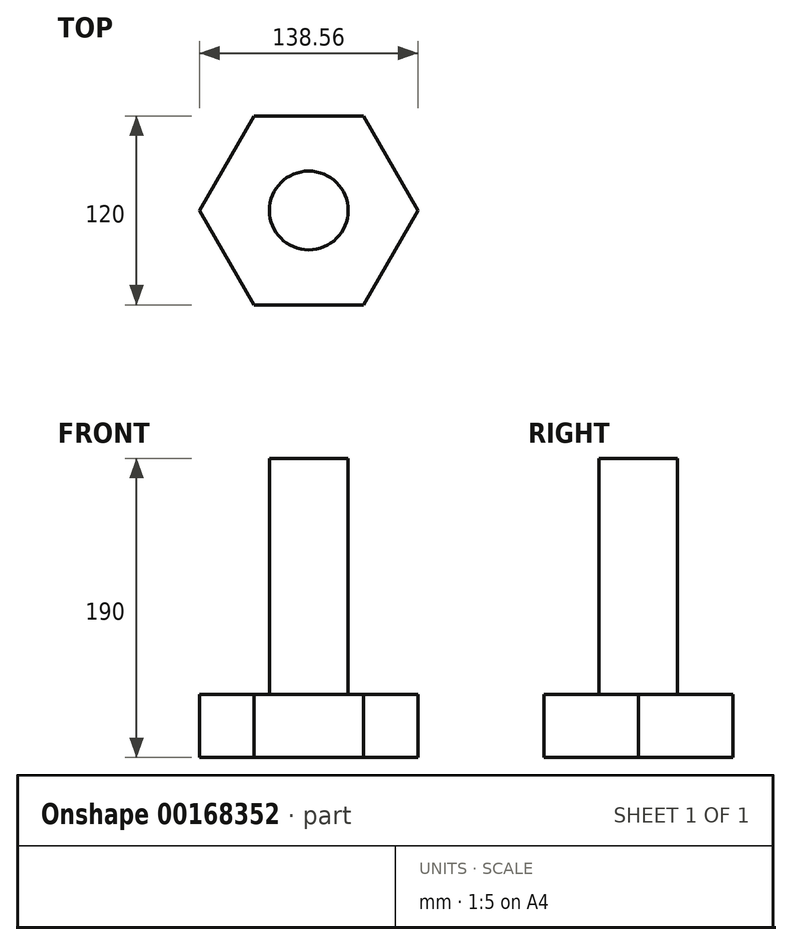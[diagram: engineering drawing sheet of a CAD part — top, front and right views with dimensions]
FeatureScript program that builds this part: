
annotation { "Feature Type Name" : "Feature", "Feature Type Description" : "" }
export const myFeature = defineFeature(function(context is Context, id is Id, definition is map)
    precondition{}
    {
        {
            var Q0;
            Q0=qCreatedBy(makeId("Top.planeOp"),FACE);
            var sketch = newSketch(context, id + "F0", { "sketchPlane" : qUnion([Q0])});
            skCircle(sketch, "E0.cCircle", {"center": v(0, 0) * mm, "radius": 60 * mm, "construction": true});
            skLineSegment(sketch, "E0.0", {"start": v(-34.64, 60) * mm, "end": v(34.64, 60) * mm});
            skLineSegment(sketch, "E0.1", {"start": v(34.64, 60) * mm, "end": v(69.28, 0) * mm});
            skLineSegment(sketch, "E0.2", {"start": v(69.28, 0) * mm, "end": v(34.64, -60) * mm});
            skLineSegment(sketch, "E0.3", {"start": v(34.64, -60) * mm, "end": v(-34.64, -60) * mm});
            skLineSegment(sketch, "E0.4", {"start": v(-34.64, -60) * mm, "end": v(-69.28, 0) * mm});
            skLineSegment(sketch, "E0.5", {"start": v(-69.28, 0) * mm, "end": v(-34.64, 60) * mm});
            skPoint(sketch, "E0.0.midPoint", {"position": v(0, 60) * mm});
            skSolve(sketch);
        }
        {
            var Q0;
            Q0=qSketchRegion(id+"F0",true);
            extrude(context, id + "F1", {"entities" : qUnion([Q0]), "depth" : 40 * mm});
        }
        {
            var Q0;
            Q0=makeQuery(id+"F1.opExtrude","CAP_FACE",FACE,{"disambiguationData":[OSD([sQuery(id+"F0.wireOp",EDGE,"E0.0"),sQuery(id+"F0.wireOp",EDGE,"E0.1"),sQuery(id+"F0.wireOp",EDGE,"E0.2"),sQuery(id+"F0.wireOp",EDGE,"E0.3"),sQuery(id+"F0.wireOp",EDGE,"E0.4"),sQuery(id+"F0.wireOp",EDGE,"E0.5")])],"isStart":false});
            var sketch = newSketch(context, id + "F2", { "sketchPlane" : qUnion([Q0])});
            skCircle(sketch, "E1", {"center": v(0, 0) * mm, "radius": 25 * mm});
            skSolve(sketch);
        }
        {
            var Q0;
            Q0=makeQuery(id+"F2.imprint","IMPRINT",FACE,{"disambiguationData":[TD([[makeQuery(id+"F2.imprint","IMPRINT",EDGE,{"derivedFrom":sQuery(id+"F2.wireOp",EDGE,"E1")}),1.0]])]});
            extrude(context, id + "F3", {"entities" : qUnion([Q0]), "operationType" : NewBodyOperationType.ADD, "depth" : 150 * mm});
        }
    });
